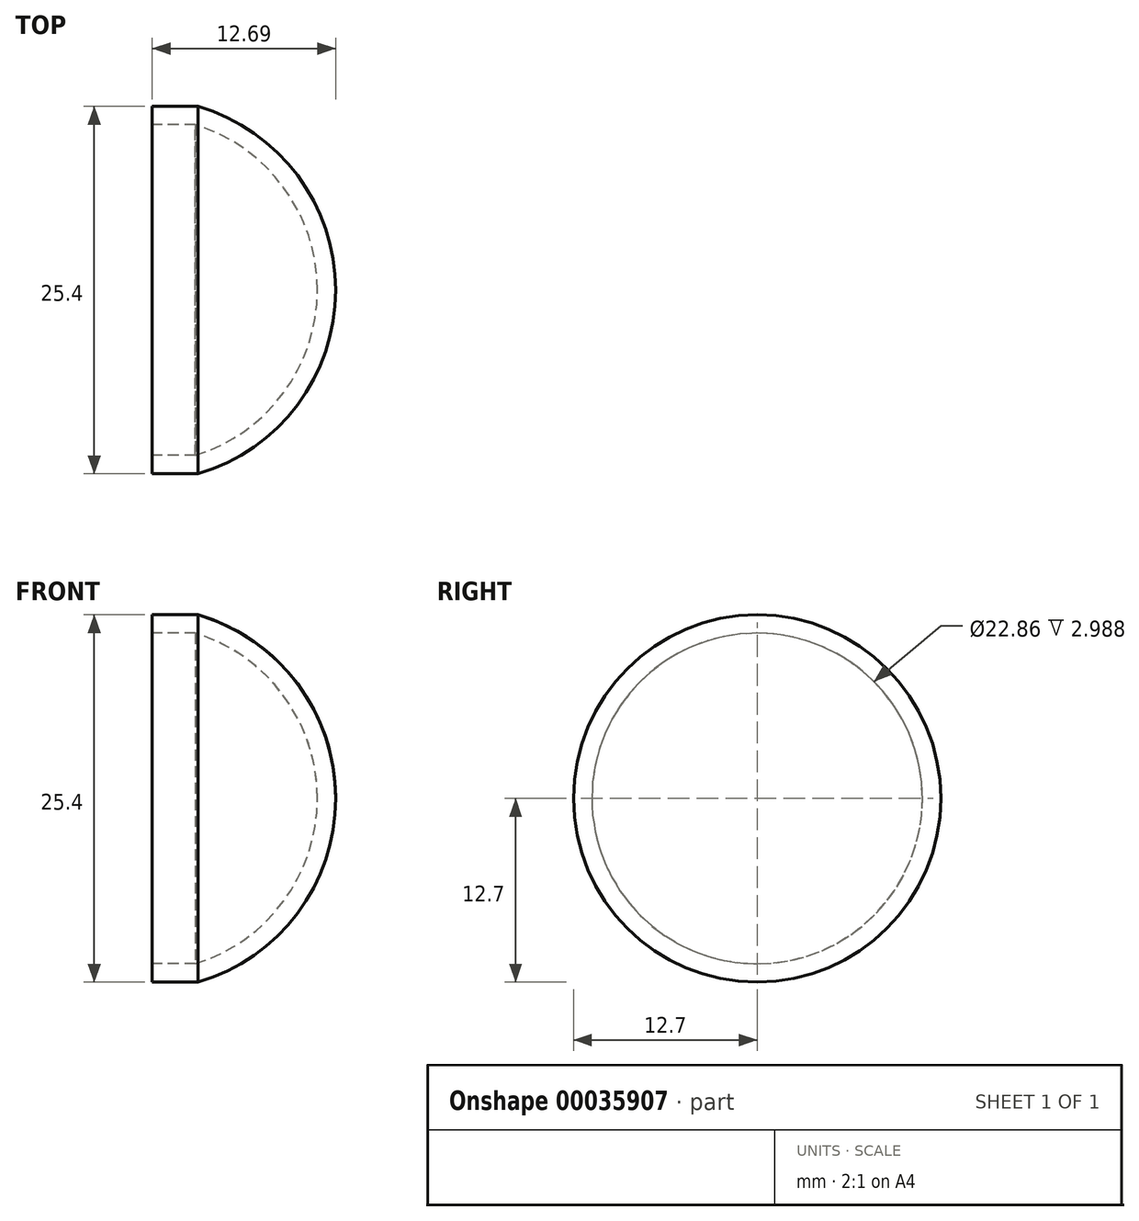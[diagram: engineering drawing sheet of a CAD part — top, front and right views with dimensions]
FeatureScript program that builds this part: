
annotation { "Feature Type Name" : "Feature", "Feature Type Description" : "" }
export const myFeature = defineFeature(function(context is Context, id is Id, definition is map)
    precondition{}
    {
        {
            var Q0;
            Q0=qCreatedBy(makeId("Front.planeOp"),FACE);
            var sketch = newSketch(context, id + "F0", { "sketchPlane" : qUnion([Q0])});
            skLineSegment(sketch, "E0", {"start": v(0, 12.7) * mm, "end": v(0, 0) * mm});
            skLineSegment(sketch, "E1", {"start": v(0, 12.7) * mm, "end": v(3.18, 12.7) * mm});
            skLineSegment(sketch, "E2", {"start": v(3.18, 12.7) * mm, "end": v(3.18, 0) * mm});
            skArc(sketch, "E3", {"start": v(12.69, 0) * mm, "mid": v(10.05, 7.93) * mm, "end": v(3.18, 12.7) * mm});
            skLineSegment(sketch, "E4", {"start": v(0, 0) * mm, "end": v(12.69, 0) * mm});
            skPoint(sketch, "E4.endSnap0", {"position": v(3.18, 0) * mm});
            skSolve(sketch);
        }
        {
            var Q0;
            Q0 = qSketchRegion(id + "F0", true);
            var Q1;
            Q1=sQuery(id+"F0.wireOp",EDGE,"E4");
            revolve(context, id + "F1", {"entities" : qUnion([Q0]), "axis" : qUnion([Q1]), "revolveType" : RevolveType.FULL});
        }
        {
            var Q0;
            Q0=makeQuery(id+"F1.opRevolve","SWEPT_FACE",FACE,{"disambiguationData":[OSD([sQuery(id+"F0.wireOp",EDGE,"E0")])]});
            shell(context, id + "F2", {"entities" : qUnion([Q0]), "thickness" : 1.27 * mm});
        }
    });
